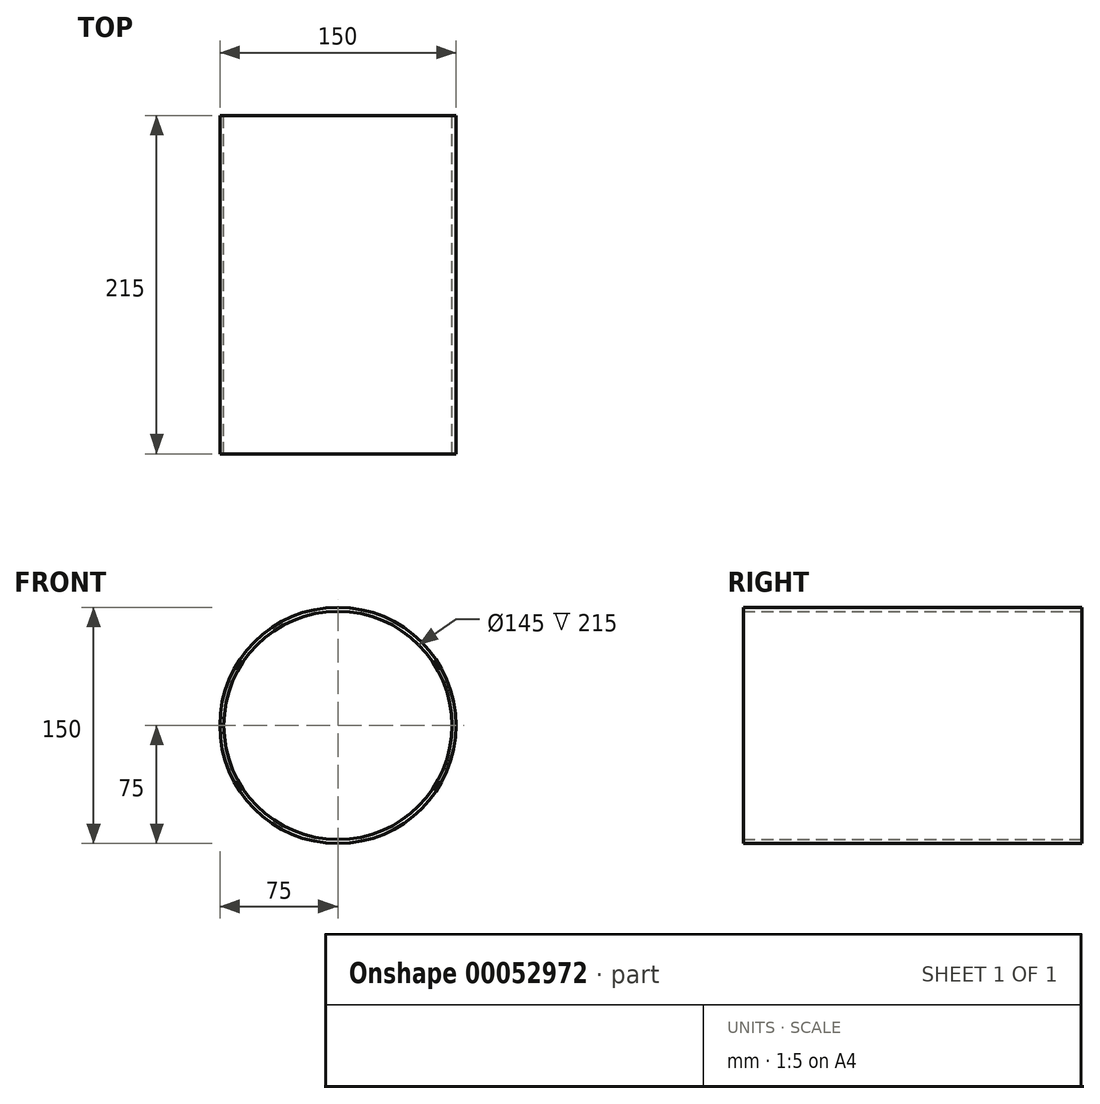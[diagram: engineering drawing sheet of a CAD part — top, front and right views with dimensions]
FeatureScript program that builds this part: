
annotation { "Feature Type Name" : "Feature", "Feature Type Description" : "" }
export const myFeature = defineFeature(function(context is Context, id is Id, definition is map)
    precondition{}
    {
        {
            var Q0;
            Q0=qCreatedBy(makeId("Front.planeOp"),FACE);
            var sketch = newSketch(context, id + "F0", { "sketchPlane" : qUnion([Q0])});
            skCircle(sketch, "E0", {"center": v(0, 0) * mm, "radius": 75 * mm});
            skCircle(sketch, "E1", {"center": v(0, 0) * mm, "radius": 4 * mm});
            skCircle(sketch, "E2", {"center": v(0, 0) * mm, "radius": 72.5 * mm});
            skSolve(sketch);
        }
        {
            var Q0;
            Q0=makeQuery(id+"F0.imprint","IMPRINT",FACE,{"disambiguationData":[TD([[makeQuery(id+"F0.imprint","IMPRINT",EDGE,{"derivedFrom":sQuery(id+"F0.wireOp",EDGE,"E0")}),1.0]])]});
            extrude(context, id + "F1", {"entities" : qUnion([Q0]), "depth" : 140 * mm});
        }
        {
            var Q0;
            Q0=makeQuery(id+"F1.opExtrude","CAP_FACE",FACE,{"disambiguationData":[OSD([sQuery(id+"F0.wireOp",EDGE,"E0"),sQuery(id+"F0.wireOp",EDGE,"E2")])],"isStart":true});
            extrude(context, id + "F2", {"entities" : qUnion([Q0]), "operationType" : NewBodyOperationType.ADD, "depth" : 75 * mm});
        }
    });
